# Revit family: Drain_Waste-JayR.Smith-Sani-Ceptor-3140-3161_Series
name_source: partatom
category: Plumbing Fixtures
revit_build: Autodesk Revit 2018 (Build: 20170223_1515(x64)
units: mm (PartAtom-declared; Revit-internal decimal feet)

## family parameters
Always vertical = No
Cut with Voids When Loaded = No
OmniClass Number = 23.45.55.21
OmniClass Title = Drains (Wastes)
Part Type = Normal
Room Calculation Point = No
Round Connector Dimension = Use Diameter
Shared = Yes
Work Plane-Based = Yes

## types (12) — shared parameters
All Duco Cast Iron Receptor -CI = No
All Galvanized Receptor -G = No
Aluminum Flat Bottom Strainer -FBS = No
Assembly Code = D2030300
Body Material = Metal-Jay R. Smith-Cast Iron
CW Connection = No
Default Elevation = 0"
Description = Sani-Ceptor® Sanitary Acid Resistant Coated Sanitary Floor and Indirect Waste Drains with Medium Receptor, Deep and Extra Deep Receptor and Square Nickel Bronze Top
Flashing Clamp -C = No
Grate Material = Metal-Jay R. Smith-Nickel Bronze
HW Connection = No
L Speedi-Set Service Weight 02(50), 03(75) & 04"(100) sizes only = No
LXH Speedi-Set Extra Heavy 02(50), 03(75) & 04"(100) sizes only = No
Less Flange (Fig. 3155, 3156 with caulk outlet only) = No
Manufacturer = Jay R. Smith
Material = Metal-Jay R. Smith-Cast Iron
Polished Aluminum Dome Bottom Strainer -PDBS = No
Price = Prices may vary. Please consult Manufacturer Representative for most up-to-date price list.
Product Documentation Link = https://www.jrsmith.com
Product Page URL = https://www.jrsmith.com
URL = https://www.jrsmith.com
Vandal Proof Screws -U = No
Vent Connection = No
Waste Connection = Yes
Width = 14"

## per-type parameters (varying)
| type | A (Pipe Size) | B - Sediment Bucket | Connection Description | Connection Type | DBS - Dome Bottom Strainer | Depth |
| 3140C02 | 2" | No | 2" Waste Outlet Connection | Caulk Outlet Connection | Yes | 6" |
| 3150C03 | 3" | No | 3" Waste Outlet Connection | Caulk Outlet Connection | Yes | 8" |
| 3160C04 | 4" | No | 4" Waste Outlet Connection | Caulk Outlet Connection | Yes | 10" |
| 3140Y02 | 2" | No | 2" Waste Outlet Connection | No-Hub Outlet Connection | Yes | 6" |
| 3150Y03 | 3" | No | 3" Waste Outlet Connection | No-Hub Outlet Connection | Yes | 8" |
| 3160Y04 | 4" | No | 4" Waste Outlet Connection | No-Hub Outlet Connection | Yes | 10" |
| 3141C02 | 2" | Yes | 2" Waste Outlet Connection | Caulk Outlet Connection | No | 6" |
| 3141Y02 | 2" | Yes | 2" Waste Outlet Connection | No-Hub Outlet Connection | No | 6" |
| 3151C03 | 3" | Yes | 3" Waste Outlet Connection | Caulk Outlet Connection | No | 8" |
| 3151Y03 | 3" | Yes | 3" Waste Outlet Connection | No-Hub Outlet Connection | No | 8" |
| 3161C04 | 4" | Yes | 4" Waste Outlet Connection | Caulk Outlet Connection | No | 10" |
| 3161Y04 | 4" | Yes | 4" Waste Outlet Connection | No-Hub Outlet Connection | No | 10" |

note: column(s) folded — value = type name in every type: Model

## geometry (parser evidence)
native form markers: Sweep x2
no freeform markers — native parametric forms only
